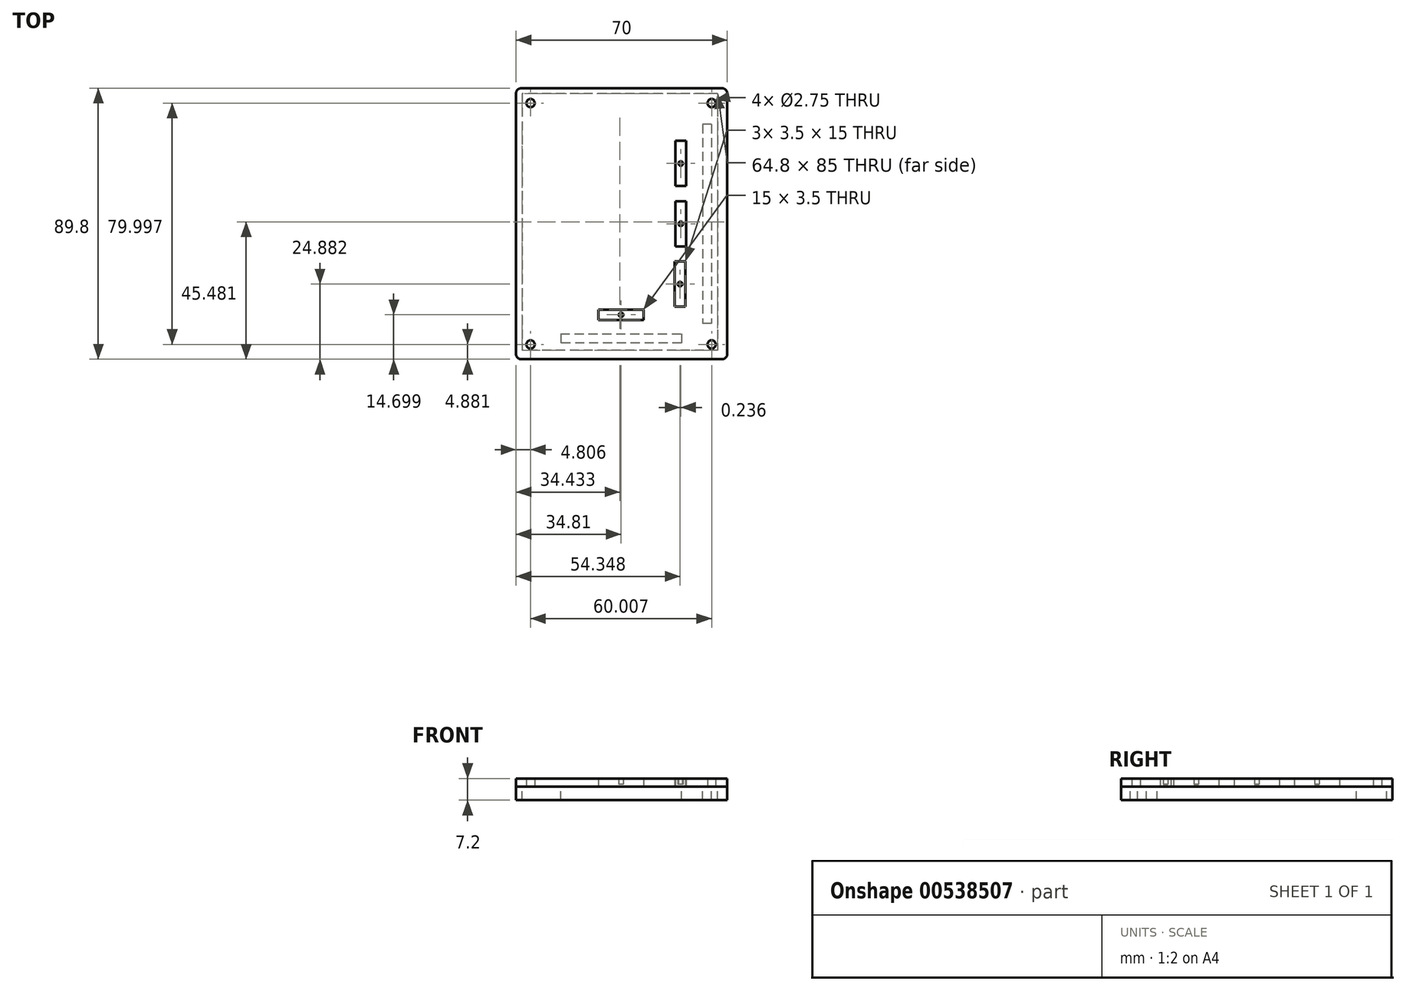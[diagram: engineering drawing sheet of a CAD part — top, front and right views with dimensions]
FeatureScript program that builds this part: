
annotation { "Feature Type Name" : "Feature", "Feature Type Description" : "" }
export const myFeature = defineFeature(function(context is Context, id is Id, definition is map)
    precondition{}
    {
        {
            var Q0;
            Q0=qCreatedBy(makeId("Top.planeOp"),FACE);
            var sketch = newSketch(context, id + "F0", { "sketchPlane" : qUnion([Q0])});
            skLineSegment(sketch, "E0.bottom", {"start": v(-33.11, 44.92) * mm, "end": v(33.49, 44.92) * mm});
            skLineSegment(sketch, "E0.top", {"start": v(-33.11, -44.88) * mm, "end": v(33.49, -44.88) * mm});
            skLineSegment(sketch, "E0.left", {"start": v(-34.81, 43.22) * mm, "end": v(-34.81, -43.18) * mm});
            skLineSegment(sketch, "E0.right", {"start": v(35.19, 43.22) * mm, "end": v(35.19, -43.18) * mm});
            skPoint(sketch, "E0.middle", {"position": v(-33.95, -33.75) * mm});
            skPoint(sketch, "E1.visualSharp", {"position": v(-34.81, 44.92) * mm});
            skArc(sketch, "E1.filletArc", {"start": v(-33.11, 44.92) * mm, "mid": v(-34.31, 44.42) * mm, "end": v(-34.81, 43.22) * mm});
            skPoint(sketch, "E2.visualSharp", {"position": v(35.19, 44.92) * mm});
            skArc(sketch, "E2.filletArc", {"start": v(35.19, 43.22) * mm, "mid": v(34.7, 44.42) * mm, "end": v(33.49, 44.92) * mm});
            skPoint(sketch, "E3.visualSharp", {"position": v(35.19, -44.88) * mm});
            skArc(sketch, "E3.filletArc", {"start": v(33.49, -44.88) * mm, "mid": v(34.7, -44.39) * mm, "end": v(35.19, -43.18) * mm});
            skPoint(sketch, "E4.visualSharp", {"position": v(-34.81, -44.88) * mm});
            skArc(sketch, "E4.filletArc", {"start": v(-34.81, -43.18) * mm, "mid": v(-34.31, -44.39) * mm, "end": v(-33.11, -44.88) * mm});
            skCircle(sketch, "E5", {"center": v(-30, 40) * mm, "radius": 1.38 * mm});
            skCircle(sketch, "E6.MirrorC", {"center": v(30, 40) * mm, "radius": 1.38 * mm});
            skCircle(sketch, "E7.MirrorC", {"center": v(-30, -40) * mm, "radius": 1.38 * mm});
            skCircle(sketch, "E8.MirrorC", {"center": v(30, -40) * mm, "radius": 1.38 * mm});
            skLineSegment(sketch, "E9.bottom", {"start": v(32.02, 43.1) * mm, "end": v(-32.78, 43.1) * mm});
            skLineSegment(sketch, "E9.top", {"start": v(32.02, -41.9) * mm, "end": v(-32.78, -41.9) * mm});
            skLineSegment(sketch, "E9.left", {"start": v(32.02, 43.1) * mm, "end": v(32.02, -41.9) * mm});
            skLineSegment(sketch, "E9.right", {"start": v(-32.78, 43.1) * mm, "end": v(-32.78, -41.9) * mm});
            skPoint(sketch, "E10.MirrorP", {"position": v(28.47, 0) * mm});
            skLineSegment(sketch, "E11.MirrorCS", {"start": v(26.97, 33) * mm, "end": v(26.97, -33) * mm});
            skLineSegment(sketch, "E12.MirrorCS", {"start": v(29.97, -33) * mm, "end": v(26.97, -33) * mm});
            skLineSegment(sketch, "E13.MirrorCS", {"start": v(29.97, 33) * mm, "end": v(29.97, -33) * mm});
            skLineSegment(sketch, "E14.MirrorCS", {"start": v(29.97, 33) * mm, "end": v(26.97, 33) * mm});
            skLineSegment(sketch, "E15.MirrorCS", {"start": v(-20, -36.5) * mm, "end": v(-20, -39.5) * mm});
            skLineSegment(sketch, "E16.MirrorCS", {"start": v(20, -36.5) * mm, "end": v(20, -39.5) * mm});
            skLineSegment(sketch, "E17.MirrorCS", {"start": v(20, -39.5) * mm, "end": v(-20, -39.5) * mm});
            skLineSegment(sketch, "E18.MirrorCS", {"start": v(-20, -36.5) * mm, "end": v(20, -36.5) * mm});
            skPoint(sketch, "E19.MirrorP", {"position": v(0, -38) * mm});
            skLineSegment(sketch, "E20.MirrorCS", {"start": v(-20, -39.5) * mm, "end": v(20, -39.5) * mm});
            skLineSegment(sketch, "E21.MirrorCS", {"start": v(20, -36.5) * mm, "end": v(-20, -36.5) * mm});
            skCircle(sketch, "E22.MirrorC", {"center": v(19.8, 0) * mm, "radius": 0.75 * mm});
            skCircle(sketch, "E23.MirrorC", {"center": v(19.8, -5) * mm, "radius": 0.75 * mm});
            skCircle(sketch, "E24.MirrorC", {"center": v(19.8, 5) * mm, "radius": 0.75 * mm});
            skLineSegment(sketch, "E25.MirrorCS", {"start": v(19.8, 0) * mm, "end": v(19.8, -5) * mm, "construction": true});
            skLineSegment(sketch, "E26.MirrorCS", {"start": v(19.8, 5) * mm, "end": v(19.8, 0) * mm, "construction": true});
            skLineSegment(sketch, "E27", {"start": v(29.97, -8.5) * mm, "end": v(32.02, -8.5) * mm, "construction": true});
            skLineSegment(sketch, "E28.bottom", {"start": v(18.06, 7.5) * mm, "end": v(21.56, 7.5) * mm});
            skLineSegment(sketch, "E28.top", {"start": v(18.06, -7.5) * mm, "end": v(21.56, -7.5) * mm});
            skLineSegment(sketch, "E28.left", {"start": v(18.06, 7.5) * mm, "end": v(18.06, -7.5) * mm});
            skLineSegment(sketch, "E28.right", {"start": v(21.56, 7.5) * mm, "end": v(21.56, -7.5) * mm});
            skCircle(sketch, "E29.MirrorC", {"center": v(19.77, 20) * mm, "radius": 0.75 * mm});
            skCircle(sketch, "E30.MirrorC", {"center": v(19.77, 15) * mm, "radius": 0.75 * mm});
            skCircle(sketch, "E31.MirrorC", {"center": v(19.77, 25) * mm, "radius": 0.75 * mm});
            skLineSegment(sketch, "E32.MirrorCS", {"start": v(19.77, 20) * mm, "end": v(19.77, 15) * mm, "construction": true});
            skLineSegment(sketch, "E33.MirrorCS", {"start": v(19.77, 25) * mm, "end": v(19.77, 20) * mm, "construction": true});
            skLineSegment(sketch, "E34.bottom", {"start": v(18.02, 27.5) * mm, "end": v(21.52, 27.5) * mm});
            skLineSegment(sketch, "E34.top", {"start": v(18.02, 12.5) * mm, "end": v(21.52, 12.5) * mm});
            skLineSegment(sketch, "E34.left", {"start": v(18.02, 27.5) * mm, "end": v(18.02, 12.5) * mm});
            skLineSegment(sketch, "E34.right", {"start": v(21.52, 27.5) * mm, "end": v(21.52, 12.5) * mm});
            skCircle(sketch, "E35.MirrorC", {"center": v(19.54, -20) * mm, "radius": 0.75 * mm});
            skCircle(sketch, "E36.MirrorC", {"center": v(19.54, -25) * mm, "radius": 0.75 * mm});
            skCircle(sketch, "E37.MirrorC", {"center": v(19.54, -15) * mm, "radius": 0.75 * mm});
            skLineSegment(sketch, "E38.MirrorCS", {"start": v(19.54, -20) * mm, "end": v(19.54, -25) * mm, "construction": true});
            skLineSegment(sketch, "E39.MirrorCS", {"start": v(19.54, -15) * mm, "end": v(19.54, -20) * mm, "construction": true});
            skLineSegment(sketch, "E40.bottom", {"start": v(17.79, -12.5) * mm, "end": v(21.29, -12.5) * mm});
            skLineSegment(sketch, "E40.top", {"start": v(17.79, -27.5) * mm, "end": v(21.29, -27.5) * mm});
            skLineSegment(sketch, "E40.left", {"start": v(17.79, -12.5) * mm, "end": v(17.79, -27.5) * mm});
            skLineSegment(sketch, "E40.right", {"start": v(21.29, -12.5) * mm, "end": v(21.29, -27.5) * mm});
            skLineSegment(sketch, "E41", {"start": v(19.8, 0) * mm, "end": v(19.77, 20) * mm, "construction": true});
            skLineSegment(sketch, "E42", {"start": v(19.8, 0) * mm, "end": v(19.54, -20) * mm, "construction": true});
            skCircle(sketch, "E43.MirrorC", {"center": v(0, -30.18) * mm, "radius": 0.75 * mm});
            skCircle(sketch, "E44.MirrorC", {"center": v(5, -30.18) * mm, "radius": 0.75 * mm});
            skCircle(sketch, "E45.MirrorC", {"center": v(-5, -30.18) * mm, "radius": 0.75 * mm});
            skLineSegment(sketch, "E46.MirrorCS", {"start": v(0, -30.18) * mm, "end": v(5, -30.18) * mm, "construction": true});
            skLineSegment(sketch, "E47.MirrorCS", {"start": v(-5, -30.18) * mm, "end": v(0, -30.18) * mm, "construction": true});
            skLineSegment(sketch, "E48.bottom", {"start": v(-7.5, -31.93) * mm, "end": v(-7.5, -28.43) * mm});
            skLineSegment(sketch, "E48.top", {"start": v(7.5, -31.93) * mm, "end": v(7.5, -28.43) * mm});
            skLineSegment(sketch, "E48.left", {"start": v(-7.5, -31.93) * mm, "end": v(7.5, -31.93) * mm});
            skLineSegment(sketch, "E48.right", {"start": v(-7.5, -28.43) * mm, "end": v(7.5, -28.43) * mm});
            skSolve(sketch);
        }
        {
            var Q0;
            Q0=makeQuery(id+"F0.imprint","IMPRINT",FACE,{"disambiguationData":[TD([[makeQuery(id+"F0.imprint","IMPRINT",EDGE,{"derivedFrom":sQuery(id+"F0.wireOp",EDGE,"E5")}),-1.0]])]});
            var Q1;
            Q1=makeQuery(id+"F0.imprint","IMPRINT",FACE,{"disambiguationData":[TD([[makeQuery(id+"F0.imprint","IMPRINT",EDGE,{"derivedFrom":sQuery(id+"F0.wireOp",EDGE,"E0.bottom")}),-1.0]])]});
            var Q2;
            Q2=makeQuery(id+"F0.imprint","IMPRINT",FACE,{"disambiguationData":[TD([[makeQuery(id+"F0.imprint","IMPRINT",EDGE,{"derivedFrom":sQuery(id+"F0.wireOp",EDGE,"b0413dd3-5413-4092-939b-53fc301a80ef5.MirrorCS")}),1.0]])]});
            var Q3;
            Q3=makeQuery(id+"F0.imprint","IMPRINT",FACE,{"disambiguationData":[TD([[makeQuery(id+"F0.imprint","IMPRINT",EDGE,{"derivedFrom":sQuery(id+"F0.wireOp",EDGE,"E11.MirrorCS")}),1.0]])]});
            var Q4;
            Q4=makeQuery(id+"F0.imprint","IMPRINT",FACE,{"disambiguationData":[TD([[makeQuery(id+"F0.imprint","IMPRINT",EDGE,{"derivedFrom":sQuery(id+"F0.wireOp",EDGE,"E16.MirrorCS")}),-1.0]])]});
            var Q5;
            Q5=makeQuery(id+"F0.imprint","IMPRINT",FACE,{"disambiguationData":[TD([[makeQuery(id+"F0.imprint","IMPRINT",EDGE,{"derivedFrom":sQuery(id+"F0.wireOp",EDGE,"yiWuV1ti-eqgB-5LEQ-MUrF-Bqq1AmZzhk0E.bottom")}),-1.0]])]});
            var Q6;
            Q6=makeQuery(id+"F0.imprint","IMPRINT",FACE,{"disambiguationData":[TD([[makeQuery(id+"F0.imprint","IMPRINT",EDGE,{"derivedFrom":sQuery(id+"F0.wireOp",EDGE,"2b39fd2e-b62f-4e7c-b596-3199fa9879292.MirrorC")}),-1.0]])]});
            var Q7;
            Q7=makeQuery(id+"F0.imprint","IMPRINT",FACE,{"disambiguationData":[TD([[makeQuery(id+"F0.imprint","IMPRINT",EDGE,{"derivedFrom":sQuery(id+"F0.wireOp",EDGE,"E43.MirrorC")}),1.0]])]});
            var Q8;
            Q8=makeQuery(id+"F0.imprint","IMPRINT",FACE,{"disambiguationData":[TD([[makeQuery(id+"F0.imprint","IMPRINT",EDGE,{"derivedFrom":sQuery(id+"F0.wireOp",EDGE,"E29.MirrorC")}),1.0]])]});
            var Q9;
            Q9=makeQuery(id+"F0.imprint","IMPRINT",FACE,{"disambiguationData":[TD([[makeQuery(id+"F0.imprint","IMPRINT",EDGE,{"derivedFrom":sQuery(id+"F0.wireOp",EDGE,"2b39fd2e-b62f-4e7c-b596-3199fa9879294.MirrorCS")}),1.0]])]});
            var Q10;
            Q10=makeQuery(id+"F0.imprint","IMPRINT",FACE,{"disambiguationData":[TD([[makeQuery(id+"F0.imprint","IMPRINT",EDGE,{"derivedFrom":sQuery(id+"F0.wireOp",EDGE,"2b39fd2e-b62f-4e7c-b596-3199fa9879290.MirrorC")}),-1.0]])]});
            var Q11;
            Q11=makeQuery(id+"F0.imprint","IMPRINT",FACE,{"disambiguationData":[TD([[makeQuery(id+"F0.imprint","IMPRINT",EDGE,{"derivedFrom":sQuery(id+"F0.wireOp",EDGE,"E22.MirrorC")}),1.0]])]});
            var Q12;
            Q12=makeQuery(id+"F0.imprint","IMPRINT",FACE,{"disambiguationData":[TD([[makeQuery(id+"F0.imprint","IMPRINT",EDGE,{"derivedFrom":sQuery(id+"F0.wireOp",EDGE,"E35.MirrorC")}),1.0]])]});
            extrude(context, id + "F1", {"entities" : qUnion([Q0, Q1, Q2, Q3, Q4, Q5, Q6, Q7, Q8, Q9, Q10, Q11, Q12]), "depth" : 2.7 * mm, "offsetDistance" : 25 * mm});
        }
        {
            var Q0;
            Q0=makeQuery(id+"F0.imprint","IMPRINT",FACE,{"disambiguationData":[TD([[makeQuery(id+"F0.imprint","IMPRINT",EDGE,{"derivedFrom":sQuery(id+"F0.wireOp",EDGE,"E0.bottom")}),-1.0]])]});
            var Q1;
            Q1=makeQuery(id+"F0.imprint","IMPRINT",FACE,{"disambiguationData":[TD([[makeQuery(id+"F0.imprint","IMPRINT",EDGE,{"derivedFrom":sQuery(id+"F0.wireOp",EDGE,"E11.MirrorCS")}),1.0]])]});
            var Q2;
            Q2=makeQuery(id+"F0.imprint","IMPRINT",FACE,{"disambiguationData":[TD([[makeQuery(id+"F0.imprint","IMPRINT",EDGE,{"derivedFrom":sQuery(id+"F0.wireOp",EDGE,"E16.MirrorCS")}),-1.0]])]});
            var Q3;
            Q3=makeQuery(id+"F0.imprint","IMPRINT",FACE,{"disambiguationData":[TD([[makeQuery(id+"F0.imprint","IMPRINT",EDGE,{"derivedFrom":sQuery(id+"F0.wireOp",EDGE,"yiWuV1ti-eqgB-5LEQ-MUrF-Bqq1AmZzhk0E.bottom")}),-1.0]])]});
            var Q4;
            Q4=makeQuery(id+"F0.imprint","IMPRINT",FACE,{"disambiguationData":[TD([[makeQuery(id+"F0.imprint","IMPRINT",EDGE,{"derivedFrom":sQuery(id+"F0.wireOp",EDGE,"b0413dd3-5413-4092-939b-53fc301a80ef5.MirrorCS")}),1.0]])]});
            extrude(context, id + "F2", {"entities" : qUnion([Q0, Q1, Q2, Q3, Q4]), "oppositeDirection" : true, "depth" : 4.5 * mm, "offsetDistance" : 25 * mm});
        }
        {
            var Q0;
            Q0=makeQuery(id+"F0.imprint","IMPRINT",FACE,{"disambiguationData":[TD([[makeQuery(id+"F0.imprint","IMPRINT",EDGE,{"derivedFrom":sQuery(id+"F0.wireOp",EDGE,"E43.MirrorC")}),1.0]])]});
            var Q1;
            Q1=makeQuery(id+"F0.imprint","IMPRINT",FACE,{"disambiguationData":[TD([[makeQuery(id+"F0.imprint","IMPRINT",EDGE,{"derivedFrom":sQuery(id+"F0.wireOp",EDGE,"E35.MirrorC")}),1.0]])]});
            var Q2;
            Q2=makeQuery(id+"F0.imprint","IMPRINT",FACE,{"disambiguationData":[TD([[makeQuery(id+"F0.imprint","IMPRINT",EDGE,{"derivedFrom":sQuery(id+"F0.wireOp",EDGE,"E22.MirrorC")}),1.0]])]});
            var Q3;
            Q3=makeQuery(id+"F0.imprint","IMPRINT",FACE,{"disambiguationData":[TD([[makeQuery(id+"F0.imprint","IMPRINT",EDGE,{"derivedFrom":sQuery(id+"F0.wireOp",EDGE,"2b39fd2e-b62f-4e7c-b596-3199fa9879294.MirrorCS")}),1.0]])]});
            var Q4;
            Q4=makeQuery(id+"F0.imprint","IMPRINT",FACE,{"disambiguationData":[TD([[makeQuery(id+"F0.imprint","IMPRINT",EDGE,{"derivedFrom":sQuery(id+"F0.wireOp",EDGE,"2b39fd2e-b62f-4e7c-b596-3199fa9879290.MirrorC")}),-1.0]])]});
            var Q5;
            Q5=makeQuery(id+"F0.imprint","IMPRINT",FACE,{"disambiguationData":[TD([[makeQuery(id+"F0.imprint","IMPRINT",EDGE,{"derivedFrom":sQuery(id+"F0.wireOp",EDGE,"E29.MirrorC")}),1.0]])]});
            var Q6;
            Q6=makeQuery(id+"F0.imprint","IMPRINT",FACE,{"disambiguationData":[TD([[makeQuery(id+"F0.imprint","IMPRINT",EDGE,{"derivedFrom":sQuery(id+"F0.wireOp",EDGE,"2b39fd2e-b62f-4e7c-b596-3199fa9879292.MirrorC")}),-1.0]])]});
            var Q7;
            Q7=makeQuery(id+"F0.imprint","IMPRINT",FACE,{"disambiguationData":[TD([[makeQuery(id+"F0.imprint","IMPRINT",EDGE,{"derivedFrom":sQuery(id+"F0.wireOp",EDGE,"2b39fd2e-b62f-4e7c-b596-3199fa98792928.MirrorC")}),1.0]])]});
            var Q8;
            Q8=makeQuery(id+"F0.imprint","IMPRINT",FACE,{"disambiguationData":[TD([[makeQuery(id+"F0.imprint","IMPRINT",EDGE,{"derivedFrom":sQuery(id+"F0.wireOp",EDGE,"E44.MirrorC")}),-1.0]])]});
            var Q9;
            Q9=makeQuery(id+"F0.imprint","IMPRINT",FACE,{"disambiguationData":[TD([[makeQuery(id+"F0.imprint","IMPRINT",EDGE,{"derivedFrom":sQuery(id+"F0.wireOp",EDGE,"2b39fd2e-b62f-4e7c-b596-3199fa9879297.MirrorC")}),1.0]])]});
            var Q10;
            Q10=makeQuery(id+"F0.imprint","IMPRINT",FACE,{"disambiguationData":[TD([[makeQuery(id+"F0.imprint","IMPRINT",EDGE,{"derivedFrom":sQuery(id+"F0.wireOp",EDGE,"2b39fd2e-b62f-4e7c-b596-3199fa9879291.MirrorC")}),1.0]])]});
            var Q11;
            Q11=makeQuery(id+"F0.imprint","IMPRINT",FACE,{"disambiguationData":[TD([[makeQuery(id+"F0.imprint","IMPRINT",EDGE,{"derivedFrom":sQuery(id+"F0.wireOp",EDGE,"E24.MirrorC")}),-1.0]])]});
            var Q12;
            Q12=makeQuery(id+"F0.imprint","IMPRINT",FACE,{"disambiguationData":[TD([[makeQuery(id+"F0.imprint","IMPRINT",EDGE,{"derivedFrom":sQuery(id+"F0.wireOp",EDGE,"2b39fd2e-b62f-4e7c-b596-3199fa98792913.MirrorC")}),1.0]])]});
            var Q13;
            Q13=makeQuery(id+"F0.imprint","IMPRINT",FACE,{"disambiguationData":[TD([[makeQuery(id+"F0.imprint","IMPRINT",EDGE,{"derivedFrom":sQuery(id+"F0.wireOp",EDGE,"E23.MirrorC")}),-1.0]])]});
            var Q14;
            Q14=makeQuery(id+"F0.imprint","IMPRINT",FACE,{"disambiguationData":[TD([[makeQuery(id+"F0.imprint","IMPRINT",EDGE,{"derivedFrom":sQuery(id+"F0.wireOp",EDGE,"2b39fd2e-b62f-4e7c-b596-3199fa98792925.MirrorC")}),1.0]])]});
            var Q15;
            Q15=makeQuery(id+"F0.imprint","IMPRINT",FACE,{"disambiguationData":[TD([[makeQuery(id+"F0.imprint","IMPRINT",EDGE,{"derivedFrom":sQuery(id+"F0.wireOp",EDGE,"2b39fd2e-b62f-4e7c-b596-3199fa9879290.MirrorC")}),1.0]])]});
            var Q16;
            Q16=makeQuery(id+"F0.imprint","IMPRINT",FACE,{"disambiguationData":[TD([[makeQuery(id+"F0.imprint","IMPRINT",EDGE,{"derivedFrom":sQuery(id+"F0.wireOp",EDGE,"2b39fd2e-b62f-4e7c-b596-3199fa9879292.MirrorC")}),1.0]])]});
            var Q17;
            Q17=makeQuery(id+"F0.imprint","IMPRINT",FACE,{"disambiguationData":[TD([[makeQuery(id+"F0.imprint","IMPRINT",EDGE,{"derivedFrom":sQuery(id+"F0.wireOp",EDGE,"E30.MirrorC")}),-1.0]])]});
            var Q18;
            Q18=makeQuery(id+"F0.imprint","IMPRINT",FACE,{"disambiguationData":[TD([[makeQuery(id+"F0.imprint","IMPRINT",EDGE,{"derivedFrom":sQuery(id+"F0.wireOp",EDGE,"E31.MirrorC")}),-1.0]])]});
            var Q19;
            Q19=makeQuery(id+"F0.imprint","IMPRINT",FACE,{"disambiguationData":[TD([[makeQuery(id+"F0.imprint","IMPRINT",EDGE,{"derivedFrom":sQuery(id+"F0.wireOp",EDGE,"E36.MirrorC")}),-1.0]])]});
            var Q20;
            Q20=makeQuery(id+"F0.imprint","IMPRINT",FACE,{"disambiguationData":[TD([[makeQuery(id+"F0.imprint","IMPRINT",EDGE,{"derivedFrom":sQuery(id+"F0.wireOp",EDGE,"E37.MirrorC")}),-1.0]])]});
            var Q21;
            Q21=makeQuery(id+"F0.imprint","IMPRINT",FACE,{"disambiguationData":[TD([[makeQuery(id+"F0.imprint","IMPRINT",EDGE,{"derivedFrom":sQuery(id+"F0.wireOp",EDGE,"E29.MirrorC")}),-1.0]])]});
            var Q22;
            Q22=makeQuery(id+"F0.imprint","IMPRINT",FACE,{"disambiguationData":[TD([[makeQuery(id+"F0.imprint","IMPRINT",EDGE,{"derivedFrom":sQuery(id+"F0.wireOp",EDGE,"E45.MirrorC")}),-1.0]])]});
            var Q23;
            Q23=makeQuery(id+"F0.imprint","IMPRINT",FACE,{"disambiguationData":[TD([[makeQuery(id+"F0.imprint","IMPRINT",EDGE,{"derivedFrom":sQuery(id+"F0.wireOp",EDGE,"E43.MirrorC")}),-1.0]])]});
            var Q24;
            Q24=makeQuery(id+"F0.imprint","IMPRINT",FACE,{"disambiguationData":[TD([[makeQuery(id+"F0.imprint","IMPRINT",EDGE,{"derivedFrom":sQuery(id+"F0.wireOp",EDGE,"E35.MirrorC")}),-1.0]])]});
            var Q25;
            Q25=makeQuery(id+"F0.imprint","IMPRINT",FACE,{"disambiguationData":[TD([[makeQuery(id+"F0.imprint","IMPRINT",EDGE,{"derivedFrom":sQuery(id+"F0.wireOp",EDGE,"2b39fd2e-b62f-4e7c-b596-3199fa98792910.MirrorC")}),1.0]])]});
            var Q26;
            Q26=makeQuery(id+"F0.imprint","IMPRINT",FACE,{"disambiguationData":[TD([[makeQuery(id+"F0.imprint","IMPRINT",EDGE,{"derivedFrom":sQuery(id+"F0.wireOp",EDGE,"E22.MirrorC")}),-1.0]])]});
            var Q27;
            Q27=makeQuery(id+"F0.imprint","IMPRINT",FACE,{"disambiguationData":[TD([[makeQuery(id+"F0.imprint","IMPRINT",EDGE,{"derivedFrom":sQuery(id+"F0.wireOp",EDGE,"2b39fd2e-b62f-4e7c-b596-3199fa9879298.MirrorC")}),1.0]])]});
            extrude(context, id + "F3", {"entities" : qUnion([Q0, Q1, Q2, Q3, Q4, Q5, Q6, Q7, Q8, Q9, Q10, Q11, Q12, Q13, Q14, Q15, Q16, Q17, Q18, Q19, Q20, Q21, Q22, Q23, Q24, Q25, Q26, Q27]), "operationType" : NewBodyOperationType.REMOVE, "depth" : 0.7 * mm, "offsetDistance" : 25 * mm});
        }
    });
